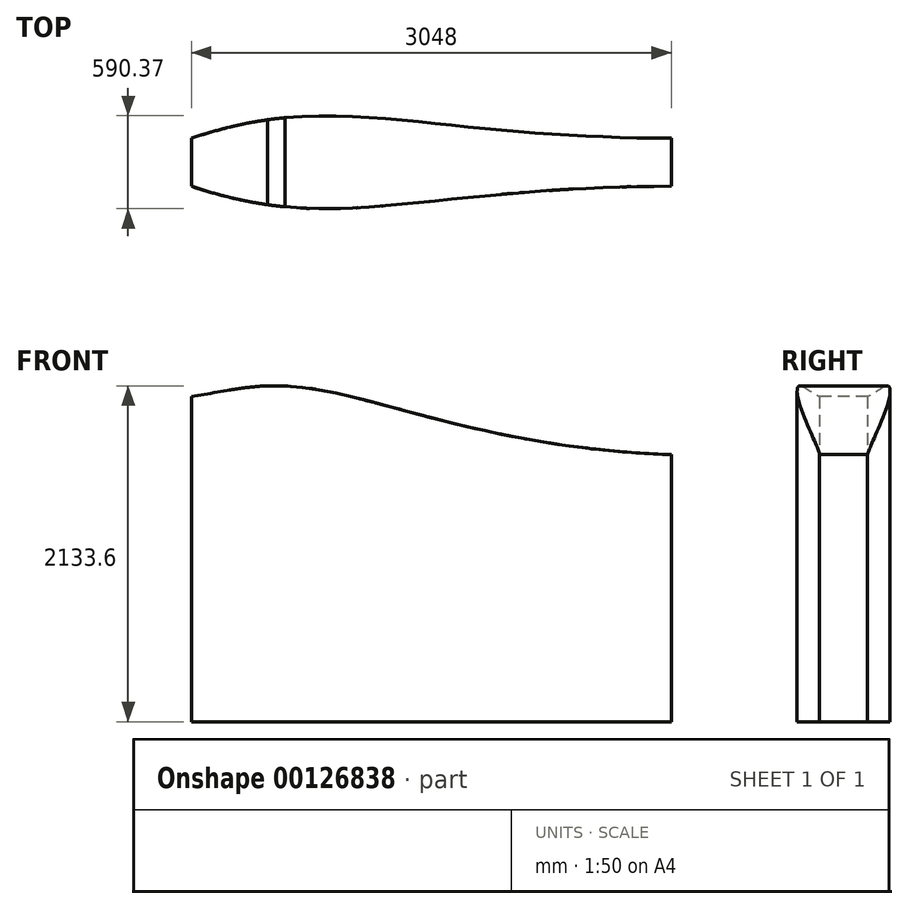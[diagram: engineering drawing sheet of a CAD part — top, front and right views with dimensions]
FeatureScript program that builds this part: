
annotation { "Feature Type Name" : "Feature", "Feature Type Description" : "" }
export const myFeature = defineFeature(function(context is Context, id is Id, definition is map)
    precondition{}
    {
        {
            var Q0;
            Q0=qCreatedBy(makeId("Top.planeOp"),FACE);
            var sketch = newSketch(context, id + "F0", { "sketchPlane" : qUnion([Q0])});
            skLineSegment(sketch, "E0", {"start": v(-1524, 152.4) * mm, "end": v(-1524, -152.4) * mm});
            skFitSpline(sketch, "E1", {"points": [v(-1524, 152.4) * mm, v(-609.6, 294.64) * mm, v(1524, 152.4) * mm], "startDerivative": vector(2304.39, 768.13) * mm, "endDerivative": vector(4926.8, -8.42) * mm});
            skLineSegment(sketch, "E2", {"start": v(1524, 152.4) * mm, "end": v(1524, -152.4) * mm});
            skFitSpline(sketch, "E3", {"points": [v(-1524, -152.4) * mm, v(-609.6, -294.64) * mm, v(1524, -152.4) * mm], "startDerivative": vector(2304.39, -768.13) * mm, "endDerivative": vector(4926.8, 0) * mm});
            skSolve(sketch);
        }
        {
            var Q0;
            Q0 = qSketchRegion(id + "F0", true);
            extrude(context, id + "F1", {"entities" : qUnion([Q0]), "depth" : 2133.6 * mm});
        }
        {
            var Q0;
            Q0=qCreatedBy(makeId("Front.planeOp"),FACE);
            var sketch = newSketch(context, id + "F2", { "sketchPlane" : qUnion([Q0])});
            skFitSpline(sketch, "E4", {"points": [v(-1905, 2032) * mm, v(-929.64, 2133.6) * mm, v(1778, 1691.64) * mm], "startDerivative": vector(2851.15, -81.46) * mm, "endDerivative": vector(6766.56, 0) * mm});
            skLineSegment(sketch, "E5", {"start": v(-1905, 2032) * mm, "end": v(-1905, 2553.8) * mm});
            skLineSegment(sketch, "E6", {"start": v(-1905, 2553.8) * mm, "end": v(1777.68, 2553.8) * mm});
            skLineSegment(sketch, "E7", {"start": v(1777.68, 2553.8) * mm, "end": v(1778, 1691.64) * mm});
            skSolve(sketch);
        }
        {
            var Q0;
            Q0 = qSketchRegion(id + "F2", true);
            extrude(context, id + "F3", {"entities" : qUnion([Q0]), "operationType" : NewBodyOperationType.REMOVE, "oppositeDirection" : true, "depth" : 543.38 * mm, "hasSecondDirection" : true, "secondDirectionOppositeDirection" : false, "secondDirectionDepth" : 650.62 * mm});
        }
    });
